# Revit family: Faucet-Kitchen-Grohe-Eurosmart_Cosmopolitan-30616_Series
name_source: partatom
category: Plumbing Fixtures
units: mm (PartAtom-declared; Revit-internal decimal feet)

## family parameters
Always vertical = No
Cut with Voids When Loaded = No
OmniClass Number = 23.45.55.14
OmniClass Title = Single Faucets
Part Type = Normal
Room Calculation Point = No
Round Connector Dimension = Use Diameter
Shared = Yes
Work Plane-Based = Yes

## types (1)
- 30616DC0
    ADA Compliant = Yes
    Aerator Height = 5 1/16"
    Assembly Code = D2020300
    CEC Compliant = Yes
    CW Connection = No
    CWFU = 1.5
    CalGreen Compliant = Yes
    Compliance Certifications = • ADA• CEC Certified• Low Lead Certified• CALGreen Compliant• Massachusetts Plumbing Board Approved• Energy Policy Act of 1992• NSF 372• NSF 61• CSA B125.1• ASME A112.18.1• Complies with lead plumbing laws
    Default Elevation = 0"
    Description = SINGLE-HANDLE SEMI-PRO DUAL SPRAY KITCHEN FAUCET 1.75 GPM
    Faucet Height = 17 15/16"
    Finish = Metal-Grohe-DC0-Super Steel Infinity Finish
    Flow Rate = 1.75 gpm (6.6 L/min)
    HW Connection = No
    HWFU = 1.5
    Installation Type = Deck-Mounted
    Manufacturer = Grohe
    Material = Metal-Grohe-DC0-Super Steel Infinity Finish
    Model = 30616DC0
    Spout Reach = 9 5/16"
    Tempered Water Connection = Yes
    Tempered Water Connection Diameter = 3/8"
    URL = http://www.grohe.com
    Vent Connection = No
    WFU = 0
    Waste Connection = No
    Width = 4 7/16"

## geometry (parser evidence)
native form markers: Sweep x3
no freeform markers — native parametric forms only
